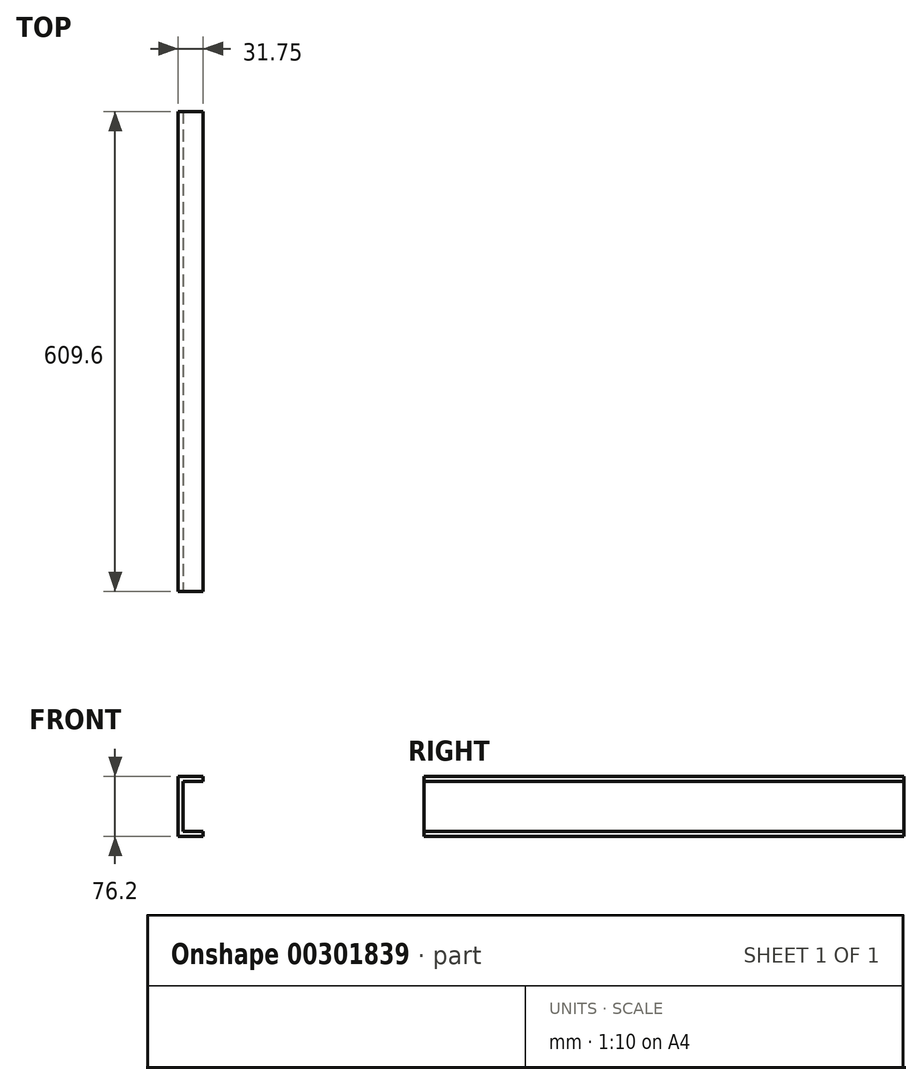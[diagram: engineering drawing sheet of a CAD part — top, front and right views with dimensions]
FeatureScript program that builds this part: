
annotation { "Feature Type Name" : "Feature", "Feature Type Description" : "" }
export const myFeature = defineFeature(function(context is Context, id is Id, definition is map)
    precondition{}
    {
        {
            var Q0;
            Q0=qCreatedBy(makeId("Front.planeOp"),FACE);
            var sketch = newSketch(context, id + "F0", { "sketchPlane" : qUnion([Q0])});
            skLineSegment(sketch, "E0", {"start": v(0, 0) * mm, "end": v(-25.4, 0) * mm});
            skLineSegment(sketch, "E1", {"start": v(-25.4, 0) * mm, "end": v(-25.4, 63.5) * mm});
            skLineSegment(sketch, "E2", {"start": v(-25.4, 63.5) * mm, "end": v(0, 63.5) * mm});
            skLineSegment(sketch, "E3", {"start": v(0, 63.5) * mm, "end": v(0, 69.85) * mm});
            skLineSegment(sketch, "E4", {"start": v(0, 69.85) * mm, "end": v(-31.75, 69.85) * mm});
            skLineSegment(sketch, "E5", {"start": v(-31.75, 69.85) * mm, "end": v(-31.75, -6.35) * mm});
            skLineSegment(sketch, "E6", {"start": v(-31.75, -6.35) * mm, "end": v(0, -6.35) * mm});
            skLineSegment(sketch, "E7", {"start": v(0, -6.35) * mm, "end": v(0, 0) * mm});
            skSolve(sketch);
        }
        {
            var Q0;
            Q0 = qSketchRegion(id + "F0", true);
            extrude(context, id + "F1", {"entities" : qUnion([Q0]), "endBound" : BoundingType.SYMMETRIC, "oppositeDirection" : true, "depth" : 609.6 * mm});
        }
    });
